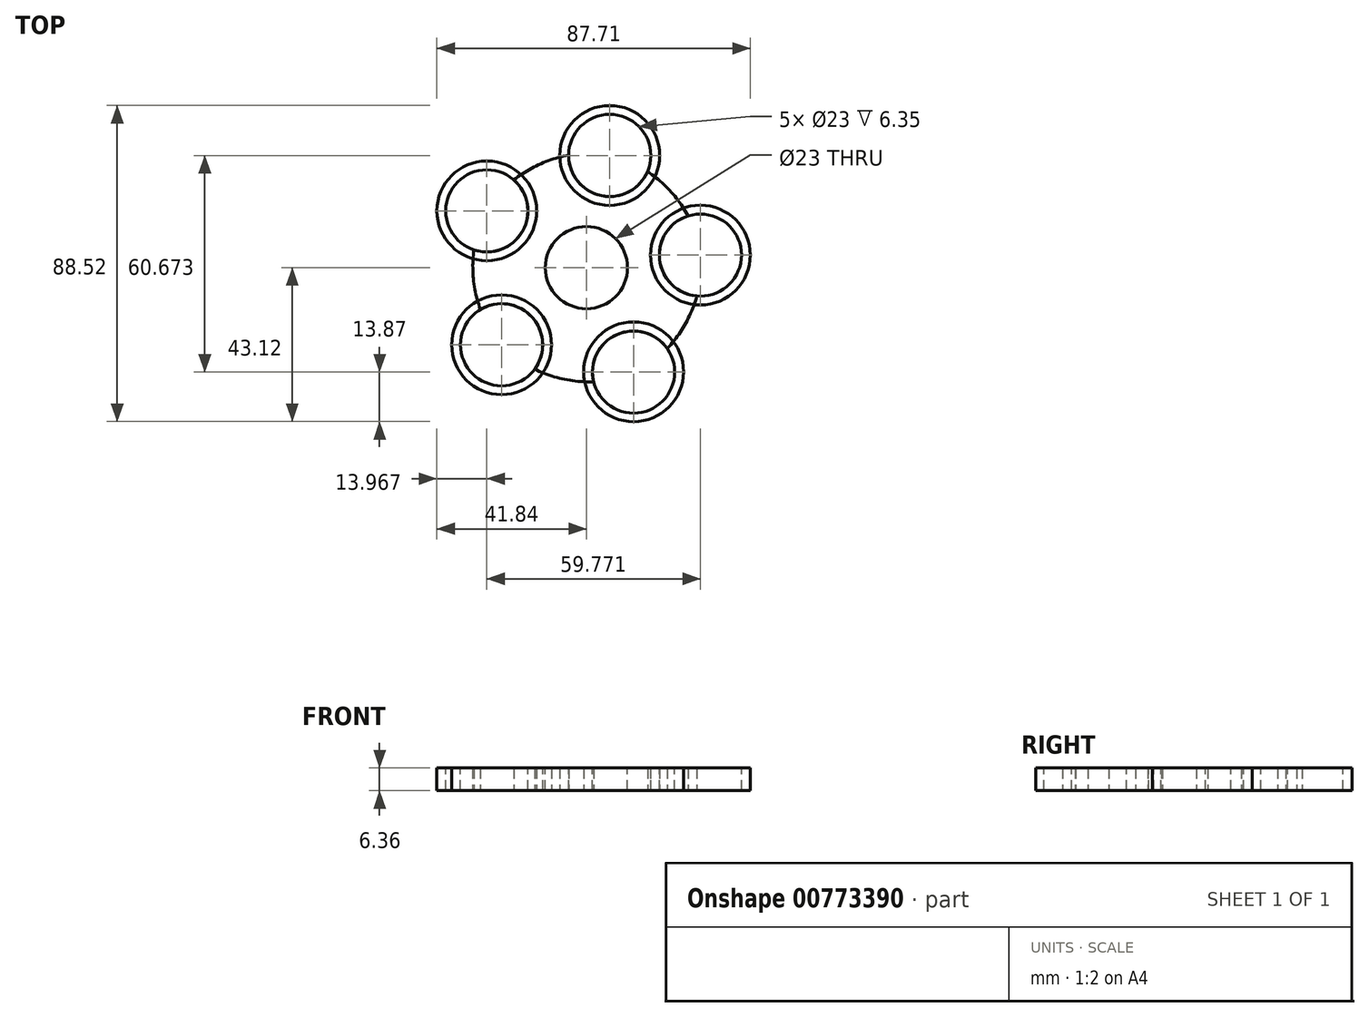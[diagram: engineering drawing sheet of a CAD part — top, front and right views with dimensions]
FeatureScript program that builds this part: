
annotation { "Feature Type Name" : "Feature", "Feature Type Description" : "" }
export const myFeature = defineFeature(function(context is Context, id is Id, definition is map)
    precondition{}
    {
        {
            var Q0;
            Q0=qCreatedBy(makeId("Top.planeOp"),FACE);
            var sketch = newSketch(context, id + "F0", { "sketchPlane" : qUnion([Q0])});
            skCircle(sketch, "E0", {"center": v(6.51, 31.42) * mm, "radius": 11.5 * mm});
            skCircle(sketch, "E1", {"center": v(31.9, 3.52) * mm, "radius": 11.5 * mm});
            skCircle(sketch, "E2", {"center": v(13.2, -29.25) * mm, "radius": 11.5 * mm});
            skCircle(sketch, "E3", {"center": v(-23.74, -21.6) * mm, "radius": 11.5 * mm});
            skCircle(sketch, "E4", {"center": v(-27.87, 15.9) * mm, "radius": 11.5 * mm});
            skCircle(sketch, "E5", {"center": v(0, 0) * mm, "radius": 11.5 * mm});
            skSolve(sketch);
        }
        {
            var Q0;
            Q0=qCreatedBy(makeId("Top.planeOp"),FACE);
            var sketch = newSketch(context, id + "F1", { "sketchPlane" : qUnion([Q0])});
            skFitSpline(sketch, "E6", {"points": [v(-27.87, 15.9) * mm, v(6.52, 31.42) * mm, v(31.9, 3.52) * mm, v(13.17, -29.42) * mm, v(-23.74, -21.6) * mm, v(-27.87, 15.9) * mm]});
            skSolve(sketch);
        }
        {
            var Q0;
            Q0=qCreatedBy(makeId("Top.planeOp"),FACE);
            var sketch = newSketch(context, id + "F2", { "sketchPlane" : qUnion([Q0])});
            skCircle(sketch, "E7", {"center": v(-23.74, -21.6) * mm, "radius": 13.97 * mm});
            skCircle(sketch, "E8", {"center": v(13.2, -29.15) * mm, "radius": 13.97 * mm});
            skCircle(sketch, "E9", {"center": v(-27.87, 15.9) * mm, "radius": 13.97 * mm});
            skCircle(sketch, "E10", {"center": v(6.51, 31.43) * mm, "radius": 13.97 * mm});
            skCircle(sketch, "E11", {"center": v(31.9, 3.52) * mm, "radius": 13.97 * mm});
            skSolve(sketch);
        }
        {
            var Q0;
            Q0 = qSketchRegion(id + "F1", true);
            var Q1;
            Q1 = qSketchRegion(id + "F2", true);
            extrude(context, id + "F3", {"entities" : qUnion([Q0, Q1]), "endBound" : BoundingType.SYMMETRIC, "depth" : 6.35 * mm, "offsetDistance" : 25.4 * mm});
        }
        {
            var Q0;
            Q0 = qSketchRegion(id + "F0", true);
            extrude(context, id + "F4", {"entities" : qUnion([Q0]), "operationType" : NewBodyOperationType.REMOVE, "endBound" : BoundingType.SYMMETRIC, "oppositeDirection" : true, "depth" : 6.35 * mm, "offsetDistance" : 25.4 * mm});
        }
    });
